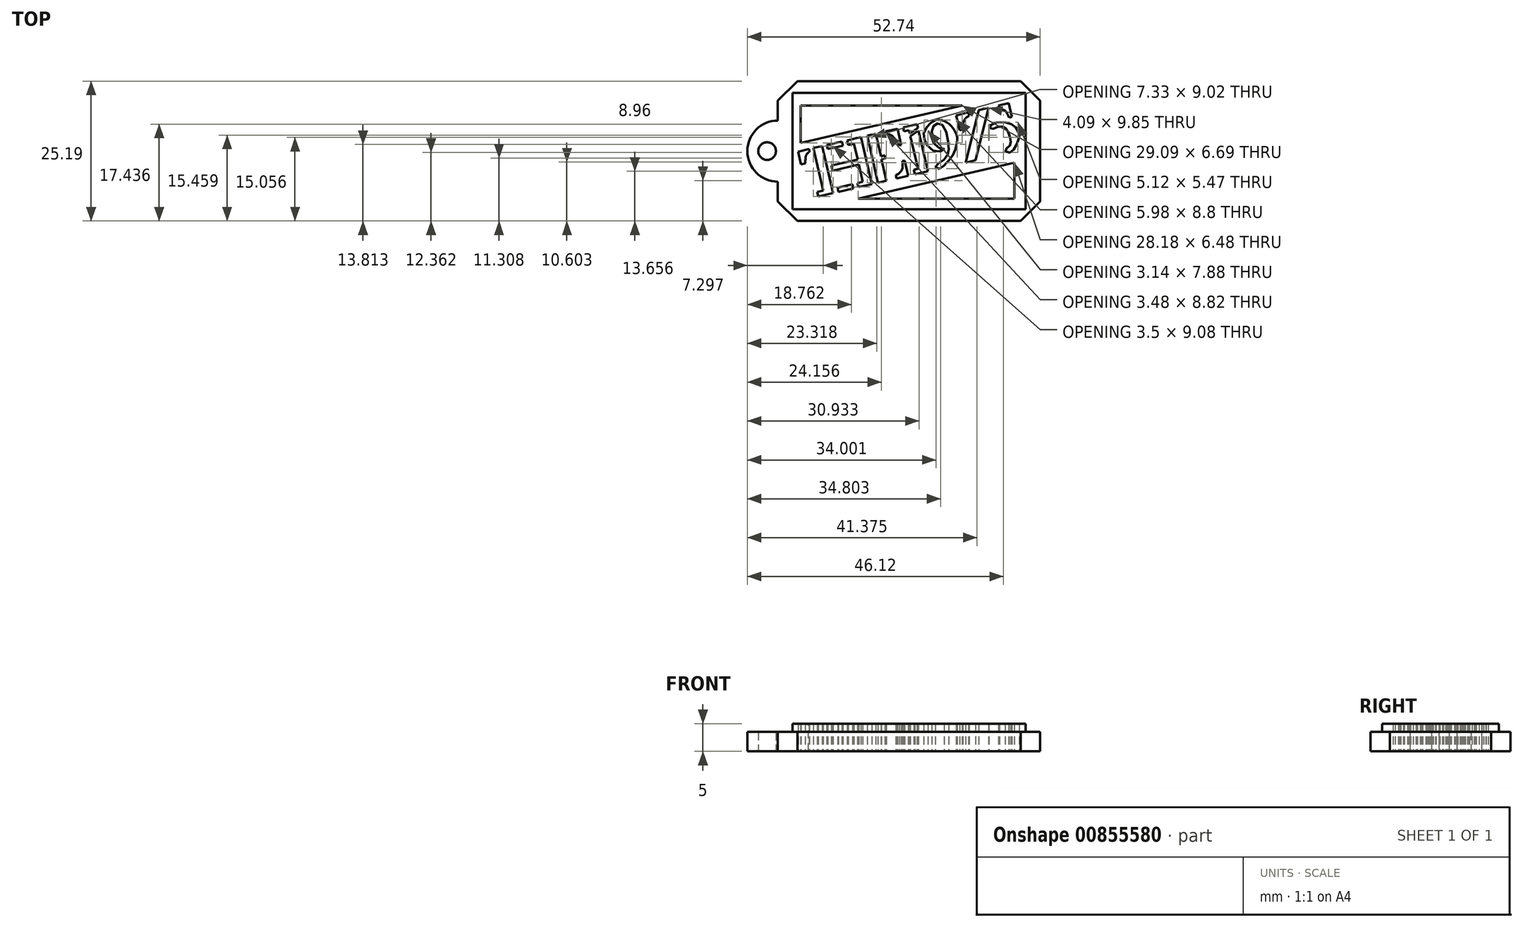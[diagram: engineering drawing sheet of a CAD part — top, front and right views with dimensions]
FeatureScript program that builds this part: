
annotation { "Feature Type Name" : "Feature", "Feature Type Description" : "" }
export const myFeature = defineFeature(function(context is Context, id is Id, definition is map)
    precondition{}
    {
        {
            var Q0;
            Q0=qCreatedBy(makeId("Top.planeOp"),FACE);
            var sketch = newSketch(context, id + "F0", { "sketchPlane" : qUnion([Q0])});
            skLineSegment(sketch, "E0.bottom", {"start": v(9.83, -52.85) * mm, "end": v(-32.17, -52.85) * mm});
            skLineSegment(sketch, "E0.top", {"start": v(9.83, -73.85) * mm, "end": v(-32.17, -73.85) * mm});
            skLineSegment(sketch, "E0.left", {"start": v(9.83, -52.85) * mm, "end": v(9.83, -73.85) * mm});
            skLineSegment(sketch, "E0.right", {"start": v(-32.17, -52.85) * mm, "end": v(-32.17, -73.85) * mm});
            skLineSegment(sketch, "E1", {"start": v(-29.18, -62.98) * mm, "end": v(-31.15, -63.44) * mm});
            skLineSegment(sketch, "E2", {"start": v(-31.15, -63.44) * mm, "end": v(-30.62, -65.75) * mm});
            skLineSegment(sketch, "E3", {"start": v(-30.62, -65.75) * mm, "end": v(-29.84, -65.57) * mm});
            skLineSegment(sketch, "E4", {"start": v(-29.18, -62.98) * mm, "end": v(-29.08, -63.43) * mm});
            skFitSpline(sketch, "E5", {"points": [v(-29.08, -63.43) * mm, v(-29.66, -63.96) * mm, v(-29.84, -64.89) * mm, v(-29.84, -65.57) * mm], "startDerivative": vector(-2.04, -1.34) * mm, "endDerivative": vector(0.02, -2.09) * mm});
            skLineSegment(sketch, "E6", {"start": v(-28.38, -62.8) * mm, "end": v(-26.83, -62.44) * mm});
            skLineSegment(sketch, "E7", {"start": v(-28.38, -62.8) * mm, "end": v(-26.62, -70.46) * mm});
            skLineSegment(sketch, "E8", {"start": v(-26.62, -70.46) * mm, "end": v(-27.73, -70.72) * mm});
            skLineSegment(sketch, "E9", {"start": v(-27.73, -70.72) * mm, "end": v(-27.55, -71.52) * mm});
            skLineSegment(sketch, "E10", {"start": v(-27.55, -71.52) * mm, "end": v(-24.88, -70.9) * mm});
            skLineSegment(sketch, "E11", {"start": v(-26.83, -62.44) * mm, "end": v(-24.88, -70.9) * mm});
            skLineSegment(sketch, "E12", {"start": v(-26, -62.25) * mm, "end": v(-25.83, -62.99) * mm});
            skLineSegment(sketch, "E13", {"start": v(-25.83, -62.99) * mm, "end": v(-23.09, -62.36) * mm});
            skLineSegment(sketch, "E14", {"start": v(-23.09, -62.36) * mm, "end": v(-23.26, -61.62) * mm});
            skLineSegment(sketch, "E15", {"start": v(-22.3, -61.4) * mm, "end": v(-22.12, -62.25) * mm});
            skLineSegment(sketch, "E16", {"start": v(-22.12, -62.25) * mm, "end": v(-21.1, -62.01) * mm});
            skLineSegment(sketch, "E17", {"start": v(-21.1, -62.01) * mm, "end": v(-20.44, -64.87) * mm});
            skLineSegment(sketch, "E18", {"start": v(-20.44, -64.87) * mm, "end": v(-25.2, -65.96) * mm});
            skLineSegment(sketch, "E19", {"start": v(-25.2, -65.96) * mm, "end": v(-24.99, -66.87) * mm});
            skLineSegment(sketch, "E20", {"start": v(-20.23, -65.77) * mm, "end": v(-19.51, -68.88) * mm});
            skLineSegment(sketch, "E21", {"start": v(-24.99, -66.87) * mm, "end": v(-20.23, -65.77) * mm});
            skLineSegment(sketch, "E22", {"start": v(-19.51, -68.88) * mm, "end": v(-20.45, -69.1) * mm});
            skLineSegment(sketch, "E23", {"start": v(-24.05, -69.92) * mm, "end": v(-23.88, -70.67) * mm});
            skLineSegment(sketch, "E24", {"start": v(-21.4, -69.3) * mm, "end": v(-21.22, -70.06) * mm});
            skLineSegment(sketch, "E25", {"start": v(-20.45, -69.1) * mm, "end": v(-20.28, -69.85) * mm});
            skLineSegment(sketch, "E26.trimOffspring", {"start": v(-21.4, -69.3) * mm, "end": v(-24.05, -69.92) * mm});
            skLineSegment(sketch, "E27.trimOffspring", {"start": v(-20.28, -69.85) * mm, "end": v(-17.86, -69.3) * mm});
            skLineSegment(sketch, "E28.trimOffspring", {"start": v(-23.88, -70.67) * mm, "end": v(-21.22, -70.06) * mm});
            skLineSegment(sketch, "E29.trimOffspring", {"start": v(-26, -62.25) * mm, "end": v(-23.26, -61.62) * mm});
            skLineSegment(sketch, "E30", {"start": v(-19.8, -60.83) * mm, "end": v(-17.86, -69.3) * mm});
            skLineSegment(sketch, "E31", {"start": v(-18.71, -60.58) * mm, "end": v(-16.77, -69.04) * mm});
            skLineSegment(sketch, "E32", {"start": v(-17.18, -60.22) * mm, "end": v(-16.25, -64.29) * mm});
            skLineSegment(sketch, "E33", {"start": v(-16.25, -64.29) * mm, "end": v(-15.52, -64.12) * mm});
            skLineSegment(sketch, "E34", {"start": v(-15.52, -64.12) * mm, "end": v(-15.4, -64.62) * mm});
            skLineSegment(sketch, "E35", {"start": v(-16.13, -64.79) * mm, "end": v(-15.23, -68.69) * mm});
            skLineSegment(sketch, "E36", {"start": v(-15.4, -64.62) * mm, "end": v(-16.13, -64.79) * mm});
            skLineSegment(sketch, "E37", {"start": v(-13.26, -59.32) * mm, "end": v(-12.58, -62.28) * mm});
            skLineSegment(sketch, "E38", {"start": v(-15.37, -59.8) * mm, "end": v(-15.25, -60.33) * mm});
            skFitSpline(sketch, "E39", {"points": [v(-15.25, -60.33) * mm, v(-14.52, -60.43) * mm, v(-13.53, -61.36) * mm, v(-12.9, -62.35) * mm], "startDerivative": vector(2.58, 0.12) * mm, "endDerivative": vector(1.58, -2.77) * mm});
            skFitSpline(sketch, "E40", {"points": [v(-13.57, -67.64) * mm, v(-13.08, -67.42) * mm, v(-12.43, -66.6) * mm, v(-12.39, -65.14) * mm], "startDerivative": vector(1.92, 0.63) * mm, "endDerivative": vector(-0.42, 3.82) * mm});
            skLineSegment(sketch, "E41", {"start": v(-12.9, -62.35) * mm, "end": v(-12.58, -62.28) * mm});
            skLineSegment(sketch, "E42", {"start": v(-12.39, -65.14) * mm, "end": v(-11.95, -65.04) * mm});
            skLineSegment(sketch, "E43.trimOffspring", {"start": v(-13.57, -67.64) * mm, "end": v(-13.42, -68.27) * mm});
            skLineSegment(sketch, "E44.trimOffspring", {"start": v(-11.95, -65.04) * mm, "end": v(-11.32, -67.79) * mm});
            skLineSegment(sketch, "E45", {"start": v(-12.24, -59.09) * mm, "end": v(-12.08, -59.78) * mm});
            skLineSegment(sketch, "E46", {"start": v(-12.08, -59.78) * mm, "end": v(-11.18, -59.58) * mm});
            skLineSegment(sketch, "E47", {"start": v(-11.18, -59.58) * mm, "end": v(-11.04, -60.2) * mm});
            skLineSegment(sketch, "E48", {"start": v(-11.04, -60.2) * mm, "end": v(-9.58, -59.17) * mm});
            skLineSegment(sketch, "E49", {"start": v(-9.58, -59.17) * mm, "end": v(-9.73, -58.51) * mm});
            skLineSegment(sketch, "E50", {"start": v(-10.93, -60.66) * mm, "end": v(-9.58, -66.53) * mm});
            skLineSegment(sketch, "E51", {"start": v(-9.58, -66.53) * mm, "end": v(-10.34, -66.7) * mm});
            skLineSegment(sketch, "E52", {"start": v(-10.34, -66.7) * mm, "end": v(-10.15, -67.52) * mm});
            skLineSegment(sketch, "E53", {"start": v(-9.47, -59.64) * mm, "end": v(-7.79, -66.98) * mm});
            skLineSegment(sketch, "E54", {"start": v(-10.93, -60.66) * mm, "end": v(-9.47, -59.64) * mm});
            skLineSegment(sketch, "E55.trimOffspring", {"start": v(-18.71, -60.58) * mm, "end": v(-17.18, -60.22) * mm});
            skLineSegment(sketch, "E56.trimOffspring", {"start": v(-22.3, -61.4) * mm, "end": v(-19.8, -60.83) * mm});
            skLineSegment(sketch, "E57.trimOffspring", {"start": v(-16.77, -69.04) * mm, "end": v(-15.23, -68.69) * mm});
            skLineSegment(sketch, "E58.trimOffspring", {"start": v(-13.42, -68.27) * mm, "end": v(-11.32, -67.79) * mm});
            skLineSegment(sketch, "E59.trimOffspring", {"start": v(-10.15, -67.52) * mm, "end": v(-7.79, -66.98) * mm});
            skLineSegment(sketch, "E60.trimOffspring", {"start": v(-15.37, -59.8) * mm, "end": v(-13.26, -59.32) * mm});
            skLineSegment(sketch, "E61.trimOffspring", {"start": v(-12.24, -59.09) * mm, "end": v(-9.73, -58.51) * mm});
            skFitSpline(sketch, "E62", {"points": [v(-5.16, -63.25) * mm, v(-6.59, -63.38) * mm, v(-8.01, -62.12) * mm, v(-8.54, -60.67) * mm, v(-8.2, -59.28) * mm, v(-7.22, -58.22) * mm, v(-6.32, -57.73) * mm, v(-4.87, -57.9) * mm, v(-3.69, -58.72) * mm, v(-2.92, -59.78) * mm, v(-2.53, -60.71) * mm, v(-2.64, -62.37) * mm, v(-3.44, -64.27) * mm, v(-4.66, -65.72) * mm, v(-5.83, -66.53) * mm, v(-6.38, -66.3) * mm, v(-6.27, -65.88) * mm, v(-5.07, -65.06) * mm, v(-4.25, -64) * mm, v(-4.03, -63.02) * mm, v(-4.34, -60.5) * mm, v(-5.32, -58.5) * mm, v(-6.27, -58.42) * mm, v(-6.84, -58.9) * mm, v(-7.04, -60.12) * mm, v(-6.72, -61.53) * mm, v(-5.88, -62.8) * mm, v(-4.87, -62.89) * mm, v(-5.16, -63.25) * mm]});
            skLineSegment(sketch, "E63", {"start": v(-2.7, -56.9) * mm, "end": v(-2.08, -59.61) * mm});
            skLineSegment(sketch, "E64", {"start": v(-2.08, -59.61) * mm, "end": v(-1.48, -59.48) * mm});
            skLineSegment(sketch, "E65", {"start": v(-0.47, -56.38) * mm, "end": v(-0.33, -57) * mm});
            skFitSpline(sketch, "E66", {"points": [v(-0.33, -57) * mm, v(-0.95, -57.38) * mm, v(-1.35, -58.08) * mm, v(-1.46, -58.94) * mm, v(-1.48, -59.48) * mm], "startDerivative": vector(-2.63, -1.29) * mm, "endDerivative": vector(-0.09, -2.33) * mm});
            skLineSegment(sketch, "E67", {"start": v(1.36, -55.96) * mm, "end": v(-0.96, -65.4) * mm});
            skLineSegment(sketch, "E68", {"start": v(0.8, -65) * mm, "end": v(3.13, -55.56) * mm});
            skLineSegment(sketch, "E69", {"start": v(6.75, -54.72) * mm, "end": v(7.31, -57.17) * mm});
            skLineSegment(sketch, "E70", {"start": v(7.31, -57.17) * mm, "end": v(6.8, -57.28) * mm});
            skLineSegment(sketch, "E71", {"start": v(4.92, -55.14) * mm, "end": v(5.1, -55.9) * mm});
            skFitSpline(sketch, "E72", {"points": [v(5.1, -55.9) * mm, v(5.79, -55.9) * mm, v(6.4, -56.43) * mm, v(6.8, -57.28) * mm], "startDerivative": vector(2.31, 0.37) * mm, "endDerivative": vector(0.93, -2.47) * mm});
            skFitSpline(sketch, "E73", {"points": [v(3.23, -59.02) * mm, v(4.39, -58.24) * mm, v(5.38, -58.13) * mm, v(7.22, -58.48) * mm, v(8.32, -59.48) * mm, v(8.64, -60.72) * mm, v(8.27, -61.93) * mm, v(7.67, -63) * mm, v(6.8, -63.62) * mm, v(6.17, -63.33) * mm, v(6.46, -62.77) * mm, v(7.06, -62.2) * mm, v(7.1, -61.2) * mm, v(6.8, -60.18) * mm, v(6.14, -59.18) * mm, v(5.1, -58.91) * mm, v(3.71, -59.34) * mm, v(3.23, -59.02) * mm]});
            skLineSegment(sketch, "E74.trimOffspring", {"start": v(-5.83, -66.53) * mm, "end": v(-5.7, -66.5) * mm});
            skLineSegment(sketch, "E75.trimOffspring", {"start": v(-6.4, -57.75) * mm, "end": v(-6.32, -57.73) * mm});
            skLineSegment(sketch, "E76.trimOffspring", {"start": v(-2.7, -56.9) * mm, "end": v(-0.47, -56.38) * mm});
            skLineSegment(sketch, "E77.trimOffspring", {"start": v(-0.96, -65.4) * mm, "end": v(0.8, -65) * mm});
            skLineSegment(sketch, "E78.trimOffspring", {"start": v(6.8, -63.62) * mm, "end": v(8.24, -63.3) * mm});
            skLineSegment(sketch, "E79.trimOffspring", {"start": v(1.36, -55.96) * mm, "end": v(3.13, -55.56) * mm});
            skLineSegment(sketch, "E80.trimOffspring", {"start": v(4.92, -55.14) * mm, "end": v(6.75, -54.72) * mm});
            skLineSegment(sketch, "E81.bottom", {"start": v(12.45, -50.75) * mm, "end": v(-34.8, -50.75) * mm});
            skLineSegment(sketch, "E81.top", {"start": v(12.45, -75.94) * mm, "end": v(-34.8, -75.94) * mm});
            skLineSegment(sketch, "E81.left", {"start": v(12.45, -50.75) * mm, "end": v(12.45, -75.94) * mm});
            skLineSegment(sketch, "E81.right", {"start": v(-34.8, -50.75) * mm, "end": v(-34.8, -75.94) * mm});
            skPoint(sketch, "E81.middle", {"position": v(-11.17, -63.35) * mm});
            skArc(sketch, "E82", {"start": v(-34.8, -57.85) * mm, "mid": v(-40.3, -63.35) * mm, "end": v(-34.8, -68.85) * mm});
            skArc(sketch, "E83.trimOffspring", {"start": v(-29.3, -63.58) * mm, "mid": v(-29.3, -63.3) * mm, "end": v(-29.3, -63.01) * mm});
            skCircle(sketch, "E84", {"center": v(-36.74, -63.35) * mm, "radius": 1.59 * mm});
            skLineSegment(sketch, "E85", {"start": v(-30.68, -61.85) * mm, "end": v(-1.59, -55.16) * mm});
            skPoint(sketch, "E85.endSnap0", {"position": v(-1.59, -56.64) * mm});
            skLineSegment(sketch, "E86", {"start": v(-1.59, -55.16) * mm, "end": v(-30.68, -55.16) * mm});
            skLineSegment(sketch, "E87", {"start": v(-30.68, -55.16) * mm, "end": v(-30.68, -61.85) * mm});
            skLineSegment(sketch, "E88", {"start": v(-20.38, -71.88) * mm, "end": v(7.8, -65.4) * mm});
            skLineSegment(sketch, "E89", {"start": v(7.8, -65.4) * mm, "end": v(7.8, -71.88) * mm});
            skLineSegment(sketch, "E90", {"start": v(7.8, -71.88) * mm, "end": v(-20.38, -71.88) * mm});
            skSolve(sketch);
        }
        {
            var Q0;
            Q0=makeQuery(id+"F0.imprint","IMPRINT",FACE,{"disambiguationData":[TD([[makeQuery(id+"F0.imprint","IMPRINT",EDGE,{"derivedFrom":sQuery(id+"F0.wireOp",EDGE,"E0.bottom")}),-1.0]])]});
            var Q1;
            {var subQ0=sQuery(id+"F0.wireOp",EDGE,"E82");Q1=makeQuery(id+"F0.imprint","IMPRINT",FACE,{"disambiguationData":[TD([[makeQuery(id+"F0.imprint","IMPRINT",EDGE,{"derivedFrom":subQ0}),1.0]])]});}
            extrude(context, id + "F1", {"entities" : qUnion([Q0, Q1]), "depth" : 3.5 * mm, "offsetDistance" : 25 * mm});
        }
        {
            var Q0;
            Q0=makeQuery(id+"F0.imprint","IMPRINT",FACE,{"disambiguationData":[TD([[makeQuery(id+"F0.imprint","IMPRINT",EDGE,{"derivedFrom":sQuery(id+"F0.wireOp",EDGE,"E0.bottom")}),1.0]])]});
            extrude(context, id + "F2", {"entities" : qUnion([Q0]), "operationType" : NewBodyOperationType.ADD, "depth" : 5 * mm, "offsetDistance" : 25 * mm});
        }
        {
            var Q0;
            Q0=makeQuery(id+"F1.opExtrude","SWEPT_EDGE",EDGE,{"disambiguationData":[OSD([sQuery(id+"F0.wireOp",EDGE,"E81.bottom"),sQuery(id+"F0.wireOp",EDGE,"E81.right")])]});
            var Q1;
            Q1=makeQuery(id+"F1.opExtrude","SWEPT_EDGE",EDGE,{"disambiguationData":[OSD([sQuery(id+"F0.wireOp",EDGE,"E81.top"),sQuery(id+"F0.wireOp",EDGE,"E81.right")])]});
            var Q2;
            Q2=makeQuery(id+"F1.opExtrude","SWEPT_EDGE",EDGE,{"disambiguationData":[OSD([sQuery(id+"F0.wireOp",EDGE,"E81.top"),sQuery(id+"F0.wireOp",EDGE,"E81.left")])]});
            var Q3;
            Q3=makeQuery(id+"F1.opExtrude","SWEPT_EDGE",EDGE,{"disambiguationData":[OSD([sQuery(id+"F0.wireOp",EDGE,"E81.bottom"),sQuery(id+"F0.wireOp",EDGE,"E81.left")])]});
            chamfer(context, id + "F3", {"entities" : qUnion([Q0, Q1, Q2, Q3]), "width" : 3.5 * mm, "tangentPropagation" : true});
        }
    });
